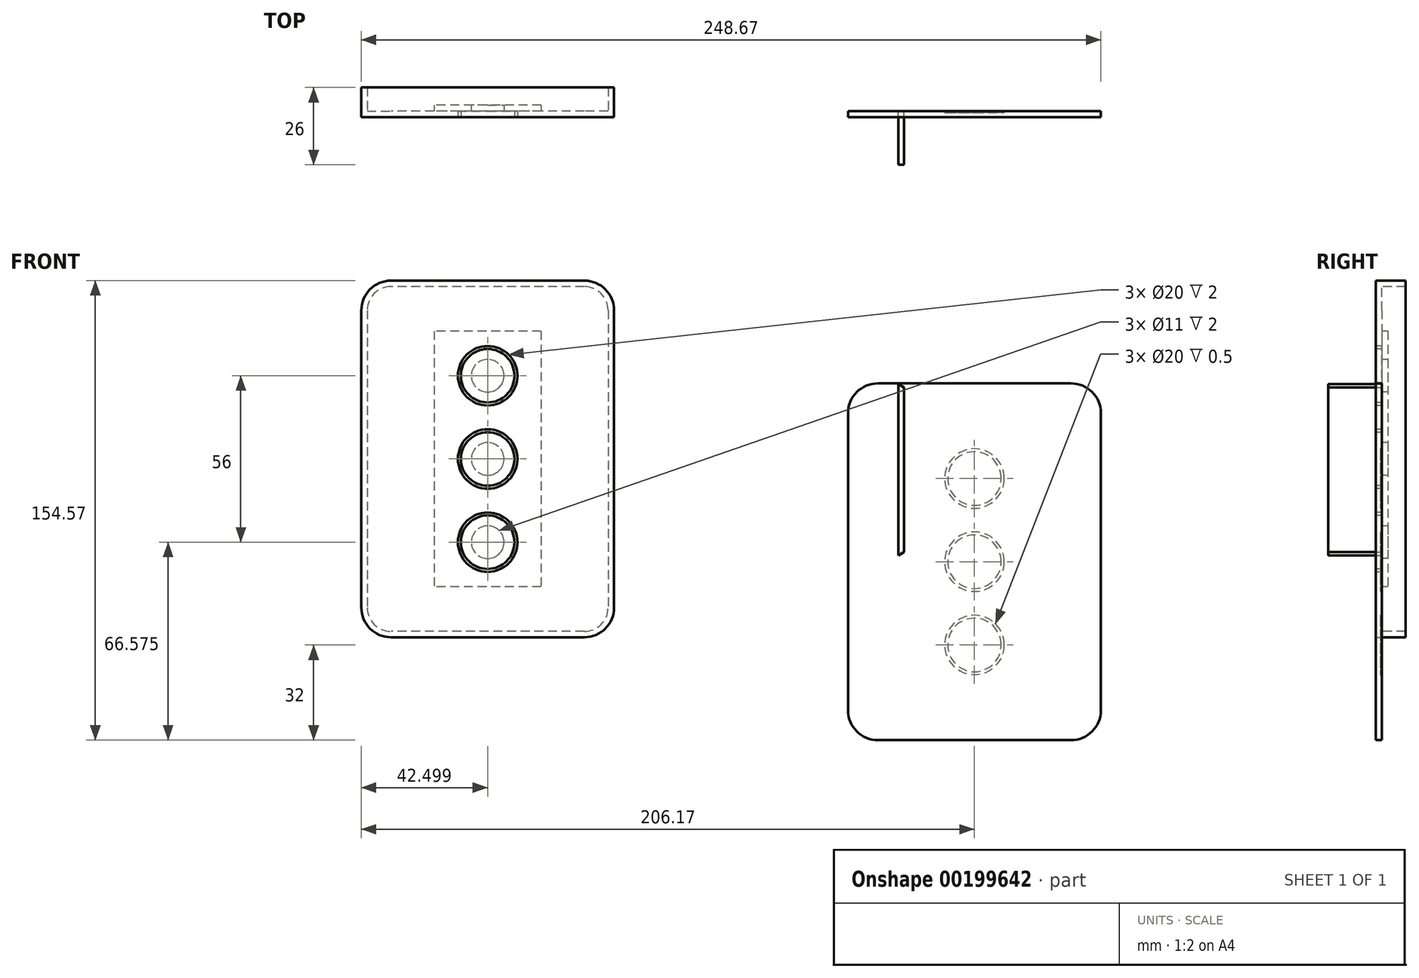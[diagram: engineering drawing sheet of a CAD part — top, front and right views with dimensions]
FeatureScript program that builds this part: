
annotation { "Feature Type Name" : "Feature", "Feature Type Description" : "" }
export const myFeature = defineFeature(function(context is Context, id is Id, definition is map)
    precondition{}
    {
        {
            var Q0;
            Q0=qCreatedBy(makeId("Front.planeOp"),FACE);
            var sketch = newSketch(context, id + "F0", { "sketchPlane" : qUnion([Q0])});
            skLineSegment(sketch, "E0.bottom", {"start": v(-32.5, 60) * mm, "end": v(32.5, 60) * mm});
            skLineSegment(sketch, "E0.top", {"start": v(-32.5, -60) * mm, "end": v(32.5, -60) * mm});
            skLineSegment(sketch, "E0.left", {"start": v(-42.5, 50) * mm, "end": v(-42.5, -50) * mm});
            skLineSegment(sketch, "E0.right", {"start": v(42.5, 50) * mm, "end": v(42.5, -50) * mm});
            skPoint(sketch, "E0.middle", {"position": v(0, 0) * mm});
            skPoint(sketch, "E1.visualSharp", {"position": v(-42.5, 60) * mm});
            skArc(sketch, "E1.filletArc", {"start": v(-32.5, 60) * mm, "mid": v(-39.57, 57.07) * mm, "end": v(-42.5, 50) * mm});
            skPoint(sketch, "E2.visualSharp", {"position": v(42.5, 60) * mm});
            skArc(sketch, "E2.filletArc", {"start": v(42.5, 50) * mm, "mid": v(39.57, 57.07) * mm, "end": v(32.5, 60) * mm});
            skPoint(sketch, "E3.visualSharp", {"position": v(42.5, -60) * mm});
            skArc(sketch, "E3.filletArc", {"start": v(32.5, -60) * mm, "mid": v(39.57, -57.07) * mm, "end": v(42.5, -50) * mm});
            skPoint(sketch, "E4.visualSharp", {"position": v(-42.5, -60) * mm});
            skArc(sketch, "E4.filletArc", {"start": v(-42.5, -50) * mm, "mid": v(-39.57, -57.07) * mm, "end": v(-32.5, -60) * mm});
            skSolve(sketch);
        }
        {
            var Q0;
            Q0=makeQuery(id+"F0.imprint","IMPRINT",FACE,{"disambiguationData":[TD([[makeQuery(id+"F0.imprint","IMPRINT",EDGE,{"derivedFrom":sQuery(id+"F0.wireOp",EDGE,"E0.bottom")}),-1.0]])]});
            extrude(context, id + "F1", {"entities" : qUnion([Q0]), "depth" : 2 * mm, "offsetDistance" : 25 * mm});
        }
        {
            var Q0;
            Q0=makeQuery(id+"F1.opExtrude","CAP_FACE",FACE,{"disambiguationData":[OSD([sQuery(id+"F0.wireOp",EDGE,"E0.bottom"),sQuery(id+"F0.wireOp",EDGE,"E0.top"),sQuery(id+"F0.wireOp",EDGE,"E0.left"),sQuery(id+"F0.wireOp",EDGE,"E0.right"),sQuery(id+"F0.wireOp",EDGE,"E1.filletArc"),sQuery(id+"F0.wireOp",EDGE,"E2.filletArc"),sQuery(id+"F0.wireOp",EDGE,"E3.filletArc"),sQuery(id+"F0.wireOp",EDGE,"E4.filletArc")])],"isStart":true});
            var sketch = newSketch(context, id + "F2", { "sketchPlane" : qUnion([Q0])});
            skCircle(sketch, "E5", {"center": v(0, 28) * mm, "radius": 10 * mm});
            skCircle(sketch, "E6", {"center": v(0, 0) * mm, "radius": 10 * mm});
            skCircle(sketch, "E7", {"center": v(0, -28) * mm, "radius": 10 * mm});
            skCircle(sketch, "E8", {"center": v(0, 28) * mm, "radius": 9 * mm});
            skCircle(sketch, "E9", {"center": v(0, 0) * mm, "radius": 9 * mm});
            skCircle(sketch, "E10", {"center": v(0, -28) * mm, "radius": 9 * mm});
            skLineSegment(sketch, "E11", {"start": v(-58.87, 60) * mm, "end": v(-58.87, -60) * mm});
            skLineSegment(sketch, "E12", {"start": v(-42.5, -66.9) * mm, "end": v(42.5, -66.9) * mm});
            skSolve(sketch);
        }
        {
            var Q0;
            Q0=makeQuery(id+"F2.imprint","IMPRINT",FACE,{"disambiguationData":[TD([[makeQuery(id+"F2.imprint","IMPRINT",EDGE,{"derivedFrom":sQuery(id+"F2.wireOp",EDGE,"E5")}),1.0]])]});
            var Q1;
            Q1=makeQuery(id+"F2.imprint","IMPRINT",FACE,{"disambiguationData":[TD([[makeQuery(id+"F2.imprint","IMPRINT",EDGE,{"derivedFrom":sQuery(id+"F2.wireOp",EDGE,"E6")}),1.0]])]});
            var Q2;
            Q2=makeQuery(id+"F2.imprint","IMPRINT",FACE,{"disambiguationData":[TD([[makeQuery(id+"F2.imprint","IMPRINT",EDGE,{"derivedFrom":sQuery(id+"F2.wireOp",EDGE,"E7")}),1.0]])]});
            extrude(context, id + "F3", {"entities" : qUnion([Q0, Q1, Q2]), "operationType" : NewBodyOperationType.REMOVE, "oppositeDirection" : true, "depth" : 0.5 * mm, "offsetDistance" : 25 * mm});
        }
        {
            var Q0;
            Q0=qCreatedBy(makeId("Front.planeOp"),FACE);
            var sketch = newSketch(context, id + "F4", { "sketchPlane" : qUnion([Q0])});
            skLineSegment(sketch, "E13", {"start": v(-25.64, 59.8) * mm, "end": v(-25.64, 2.07) * mm});
            skLineSegment(sketch, "E14", {"start": v(-23.64, 58.65) * mm, "end": v(-23.64, 3.23) * mm});
            skLineSegment(sketch, "E15", {"start": v(-23.64, 58.65) * mm, "end": v(-25.64, 59.8) * mm});
            skLineSegment(sketch, "E16", {"start": v(-25.64, 2.07) * mm, "end": v(-23.64, 3.23) * mm});
            skSolve(sketch);
        }
        {
            var Q0;
            Q0 = qSketchRegion(id + "F4", true);
            extrude(context, id + "F5", {"entities" : qUnion([Q0]), "depth" : 18 * mm, "offsetDistance" : 25 * mm});
        }
        {
            var Q0;
            Q0=qCreatedBy(makeId("Front.planeOp"),FACE);
            var sketch = newSketch(context, id + "F6", { "sketchPlane" : qUnion([Q0])});
            skLineSegment(sketch, "E17.bottom", {"start": v(-131.17, 94.57) * mm, "end": v(-196.17, 94.57) * mm});
            skLineSegment(sketch, "E17.top", {"start": v(-131.17, -25.43) * mm, "end": v(-196.17, -25.43) * mm});
            skLineSegment(sketch, "E17.left", {"start": v(-121.17, 84.57) * mm, "end": v(-121.17, -15.43) * mm});
            skLineSegment(sketch, "E17.right", {"start": v(-206.17, 84.57) * mm, "end": v(-206.17, -15.43) * mm});
            skArc(sketch, "E18.filletArc", {"start": v(-121.17, 84.57) * mm, "mid": v(-124.1, 91.65) * mm, "end": v(-131.17, 94.57) * mm});
            skArc(sketch, "E19.filletArc", {"start": v(-196.17, 94.57) * mm, "mid": v(-203.24, 91.65) * mm, "end": v(-206.17, 84.57) * mm});
            skArc(sketch, "E20.filletArc", {"start": v(-206.17, -15.43) * mm, "mid": v(-203.24, -22.5) * mm, "end": v(-196.17, -25.43) * mm});
            skArc(sketch, "E21.filletArc", {"start": v(-131.17, -25.43) * mm, "mid": v(-124.1, -22.5) * mm, "end": v(-121.17, -15.43) * mm});
            skSolve(sketch);
        }
        {
            var Q0;
            Q0=makeQuery(id+"F6.imprint","IMPRINT",FACE,{"disambiguationData":[TD([[makeQuery(id+"F6.imprint","IMPRINT",EDGE,{"derivedFrom":sQuery(id+"F6.wireOp",EDGE,"E17.bottom")}),1.0]])]});
            extrude(context, id + "F7", {"entities" : qUnion([Q0]), "depth" : 2 * mm, "offsetDistance" : 25 * mm});
        }
        {
            var Q0;
            Q0=makeQuery(id+"F7.opExtrude","CAP_FACE",FACE,{"disambiguationData":[OSD([sQuery(id+"F6.wireOp",EDGE,"E17.bottom"),sQuery(id+"F6.wireOp",EDGE,"E17.top"),sQuery(id+"F6.wireOp",EDGE,"E17.left"),sQuery(id+"F6.wireOp",EDGE,"E17.right"),sQuery(id+"F6.wireOp",EDGE,"E18.filletArc"),sQuery(id+"F6.wireOp",EDGE,"E19.filletArc"),sQuery(id+"F6.wireOp",EDGE,"E20.filletArc"),sQuery(id+"F6.wireOp",EDGE,"E21.filletArc")])],"isStart":true});
            var sketch = newSketch(context, id + "F8", { "sketchPlane" : qUnion([Q0])});
            skLineSegment(sketch, "E22.bottom", {"start": v(131.17, 92.57) * mm, "end": v(196.17, 92.57) * mm});
            skLineSegment(sketch, "E22.top", {"start": v(131.17, -23.43) * mm, "end": v(196.17, -23.43) * mm});
            skLineSegment(sketch, "E22.left", {"start": v(123.17, 84.57) * mm, "end": v(123.17, -15.43) * mm});
            skLineSegment(sketch, "E22.right", {"start": v(204.17, 84.57) * mm, "end": v(204.17, -15.43) * mm});
            skArc(sketch, "E23.filletArc", {"start": v(131.17, 92.57) * mm, "mid": v(125.51, 90.23) * mm, "end": v(123.17, 84.57) * mm});
            skArc(sketch, "E24.filletArc", {"start": v(204.17, 84.57) * mm, "mid": v(201.83, 90.23) * mm, "end": v(196.17, 92.57) * mm});
            skArc(sketch, "E25.filletArc", {"start": v(196.17, -23.43) * mm, "mid": v(201.83, -21.08) * mm, "end": v(204.17, -15.43) * mm});
            skArc(sketch, "E26.filletArc", {"start": v(123.17, -15.43) * mm, "mid": v(125.51, -21.08) * mm, "end": v(131.17, -23.43) * mm});
            skSolve(sketch);
        }
        {
            var Q0;
            Q0=makeQuery(id+"F8.imprint","IMPRINT",FACE,{"disambiguationData":[TD([[makeQuery(id+"F8.imprint","IMPRINT",EDGE,{"derivedFrom":sQuery(id+"F8.wireOp",EDGE,"E22.bottom")}),1.0]])]});
            extrude(context, id + "F9", {"entities" : qUnion([Q0]), "operationType" : NewBodyOperationType.ADD, "depth" : 8 * mm, "offsetDistance" : 25 * mm});
        }
        {
            var Q0;
            Q0=makeQuery(id+"F7.opExtrude","CAP_FACE",FACE,{"disambiguationData":[OSD([sQuery(id+"F6.wireOp",EDGE,"E17.bottom"),sQuery(id+"F6.wireOp",EDGE,"E17.top"),sQuery(id+"F6.wireOp",EDGE,"E17.left"),sQuery(id+"F6.wireOp",EDGE,"E17.right"),sQuery(id+"F6.wireOp",EDGE,"E18.filletArc"),sQuery(id+"F6.wireOp",EDGE,"E19.filletArc"),sQuery(id+"F6.wireOp",EDGE,"E20.filletArc"),sQuery(id+"F6.wireOp",EDGE,"E21.filletArc")])],"isStart":false});
            var sketch = newSketch(context, id + "F10", { "sketchPlane" : qUnion([Q0])});
            skCircle(sketch, "E27", {"center": v(-163.67, 62.57) * mm, "radius": 9 * mm});
            skCircle(sketch, "E28", {"center": v(-163.67, 34.57) * mm, "radius": 9 * mm});
            skCircle(sketch, "E29", {"center": v(-163.67, 6.57) * mm, "radius": 9 * mm});
            skCircle(sketch, "E30", {"center": v(-163.67, 62.57) * mm, "radius": 10 * mm});
            skCircle(sketch, "E31", {"center": v(-163.67, 34.57) * mm, "radius": 10 * mm});
            skCircle(sketch, "E32", {"center": v(-163.67, 6.57) * mm, "radius": 10 * mm});
            skSolve(sketch);
        }
        {
            var Q0;
            Q0 = qSketchRegion(id + "F10", true);
            extrude(context, id + "F11", {"entities" : qUnion([Q0]), "operationType" : NewBodyOperationType.REMOVE, "oppositeDirection" : true, "depth" : 25 * mm, "offsetDistance" : 25 * mm});
        }
        {
            var Q0;
            Q0=makeQuery(id+"F11.boolean.opBoolean","SPLIT",FACE,{"disambiguationData":[TD([makeQuery(id+"F9.opExtrude","SWEPT_FACE",FACE,{"disambiguationData":[OSD([sQuery(id+"F8.wireOp",EDGE,"E22.bottom")])]})])],"derivedFrom":makeQuery(id+"F7.opExtrude","CAP_FACE",FACE,{"disambiguationData":[OSD([sQuery(id+"F6.wireOp",EDGE,"E17.bottom"),sQuery(id+"F6.wireOp",EDGE,"E17.top"),sQuery(id+"F6.wireOp",EDGE,"E17.left"),sQuery(id+"F6.wireOp",EDGE,"E17.right"),sQuery(id+"F6.wireOp",EDGE,"E18.filletArc"),sQuery(id+"F6.wireOp",EDGE,"E19.filletArc"),sQuery(id+"F6.wireOp",EDGE,"E20.filletArc"),sQuery(id+"F6.wireOp",EDGE,"E21.filletArc")])],"isStart":true})});
            var sketch = newSketch(context, id + "F12", { "sketchPlane" : qUnion([Q0])});
            skLineSegment(sketch, "E33.bottom", {"start": v(145.67, 77.57) * mm, "end": v(181.67, 77.57) * mm});
            skLineSegment(sketch, "E33.top", {"start": v(145.67, -8.43) * mm, "end": v(181.67, -8.43) * mm});
            skLineSegment(sketch, "E33.left", {"start": v(145.67, 77.57) * mm, "end": v(145.67, -8.43) * mm});
            skLineSegment(sketch, "E33.right", {"start": v(181.67, 77.57) * mm, "end": v(181.67, -8.43) * mm});
            skPoint(sketch, "E34.start.orphan", {"position": v(163.67, 62.57) * mm});
            skPoint(sketch, "E35.end.orphan", {"position": v(163.67, -8.43) * mm});
            skPoint(sketch, "E35.start.orphan", {"position": v(163.67, 6.57) * mm});
            skSolve(sketch);
        }
        {
            var Q0;
            Q0=makeQuery(id+"F12.imprint","IMPRINT",FACE,{"disambiguationData":[TD([[makeQuery(id+"F12.imprint","IMPRINT",EDGE,{"derivedFrom":makeQuery(id+"F11.boolean.opBoolean","INTERSECT",EDGE,{"derivedFrom":[makeQuery(id+"F7.opExtrude","CAP_FACE",FACE,{"disambiguationData":[OSD([sQuery(id+"F6.wireOp",EDGE,"E17.bottom"),sQuery(id+"F6.wireOp",EDGE,"E17.top"),sQuery(id+"F6.wireOp",EDGE,"E17.left"),sQuery(id+"F6.wireOp",EDGE,"E17.right"),sQuery(id+"F6.wireOp",EDGE,"E18.filletArc"),sQuery(id+"F6.wireOp",EDGE,"E19.filletArc"),sQuery(id+"F6.wireOp",EDGE,"E20.filletArc"),sQuery(id+"F6.wireOp",EDGE,"E21.filletArc")])],"isStart":true}),makeQuery(id+"F11.opExtrude","SWEPT_FACE",FACE,{"disambiguationData":[OSD([sQuery(id+"F10.wireOp",EDGE,"E30")])]})]})}),-1.0]])]});
            var Q1;
            Q1=makeQuery(id+"F12.imprint","IMPRINT",FACE,{"disambiguationData":[TD([[makeQuery(id+"F12.imprint","IMPRINT",EDGE,{"derivedFrom":makeQuery(id+"F11.boolean.opBoolean","INTERSECT",EDGE,{"derivedFrom":[makeQuery(id+"F7.opExtrude","CAP_FACE",FACE,{"disambiguationData":[OSD([sQuery(id+"F6.wireOp",EDGE,"E17.bottom"),sQuery(id+"F6.wireOp",EDGE,"E17.top"),sQuery(id+"F6.wireOp",EDGE,"E17.left"),sQuery(id+"F6.wireOp",EDGE,"E17.right"),sQuery(id+"F6.wireOp",EDGE,"E18.filletArc"),sQuery(id+"F6.wireOp",EDGE,"E19.filletArc"),sQuery(id+"F6.wireOp",EDGE,"E20.filletArc"),sQuery(id+"F6.wireOp",EDGE,"E21.filletArc")])],"isStart":true}),makeQuery(id+"F11.opExtrude","SWEPT_FACE",FACE,{"disambiguationData":[OSD([sQuery(id+"F10.wireOp",EDGE,"E31")])]})]})}),-1.0]])]});
            var Q2;
            Q2=makeQuery(id+"F12.imprint","IMPRINT",FACE,{"disambiguationData":[TD([[makeQuery(id+"F12.imprint","IMPRINT",EDGE,{"derivedFrom":makeQuery(id+"F11.boolean.opBoolean","INTERSECT",EDGE,{"derivedFrom":[makeQuery(id+"F7.opExtrude","CAP_FACE",FACE,{"disambiguationData":[OSD([sQuery(id+"F6.wireOp",EDGE,"E17.bottom"),sQuery(id+"F6.wireOp",EDGE,"E17.top"),sQuery(id+"F6.wireOp",EDGE,"E17.left"),sQuery(id+"F6.wireOp",EDGE,"E17.right"),sQuery(id+"F6.wireOp",EDGE,"E18.filletArc"),sQuery(id+"F6.wireOp",EDGE,"E19.filletArc"),sQuery(id+"F6.wireOp",EDGE,"E20.filletArc"),sQuery(id+"F6.wireOp",EDGE,"E21.filletArc")])],"isStart":true}),makeQuery(id+"F11.opExtrude","SWEPT_FACE",FACE,{"disambiguationData":[OSD([sQuery(id+"F10.wireOp",EDGE,"E32")])]})]})}),-1.0]])]});
            var Q3;
            Q3=makeQuery(id+"F12.imprint","IMPRINT",FACE,{"disambiguationData":[TD([[makeQuery(id+"F12.imprint","IMPRINT",EDGE,{"derivedFrom":sQuery(id+"F12.wireOp",EDGE,"E33.bottom")}),-1.0]])]});
            extrude(context, id + "F13", {"entities" : qUnion([Q0, Q1, Q2, Q3]), "operationType" : NewBodyOperationType.ADD, "depth" : 2 * mm, "offsetDistance" : 25 * mm});
        }
        {
            var Q0;
            Q0=makeQuery(id+"F13.boolean.opBoolean","SPLIT",FACE,{"disambiguationData":[TD([makeQuery(id+"F11.boolean.opBoolean","COPY",FACE,{"derivedFrom":makeQuery(id+"F11.opExtrude","SWEPT_FACE",FACE,{"disambiguationData":[OSD([sQuery(id+"F10.wireOp",EDGE,"E30")])]})})])],"derivedFrom":makeQuery(id+"F13.opExtrude","CAP_FACE",FACE,{"disambiguationData":[OSD([sQuery(id+"F12.wireOp",EDGE,"E33.bottom"),sQuery(id+"F12.wireOp",EDGE,"E33.top"),sQuery(id+"F12.wireOp",EDGE,"E33.left"),sQuery(id+"F12.wireOp",EDGE,"E33.right")])],"isStart":true})});
            var sketch = newSketch(context, id + "F14", { "sketchPlane" : qUnion([Q0])});
            skCircle(sketch, "E36", {"center": v(-163.67, 62.57) * mm, "radius": 5.5 * mm});
            skSolve(sketch);
        }
        {
            var Q0;
            Q0=makeQuery(id+"F13.boolean.opBoolean","SPLIT",FACE,{"disambiguationData":[TD([makeQuery(id+"F11.boolean.opBoolean","COPY",FACE,{"derivedFrom":makeQuery(id+"F11.opExtrude","SWEPT_FACE",FACE,{"disambiguationData":[OSD([sQuery(id+"F10.wireOp",EDGE,"E31")])]})})])],"derivedFrom":makeQuery(id+"F13.opExtrude","CAP_FACE",FACE,{"disambiguationData":[OSD([sQuery(id+"F12.wireOp",EDGE,"E33.bottom"),sQuery(id+"F12.wireOp",EDGE,"E33.top"),sQuery(id+"F12.wireOp",EDGE,"E33.left"),sQuery(id+"F12.wireOp",EDGE,"E33.right")])],"isStart":true})});
            var sketch = newSketch(context, id + "F15", { "sketchPlane" : qUnion([Q0])});
            skCircle(sketch, "E37", {"center": v(-163.67, 34.57) * mm, "radius": 5.5 * mm});
            skSolve(sketch);
        }
        {
            var Q0;
            Q0=makeQuery(id+"F13.boolean.opBoolean","SPLIT",FACE,{"disambiguationData":[TD([makeQuery(id+"F11.boolean.opBoolean","COPY",FACE,{"derivedFrom":makeQuery(id+"F11.opExtrude","SWEPT_FACE",FACE,{"disambiguationData":[OSD([sQuery(id+"F10.wireOp",EDGE,"E32")])]})})])],"derivedFrom":makeQuery(id+"F13.opExtrude","CAP_FACE",FACE,{"disambiguationData":[OSD([sQuery(id+"F12.wireOp",EDGE,"E33.bottom"),sQuery(id+"F12.wireOp",EDGE,"E33.top"),sQuery(id+"F12.wireOp",EDGE,"E33.left"),sQuery(id+"F12.wireOp",EDGE,"E33.right")])],"isStart":true})});
            var sketch = newSketch(context, id + "F16", { "sketchPlane" : qUnion([Q0])});
            skCircle(sketch, "E38", {"center": v(-163.67, 6.57) * mm, "radius": 5.5 * mm});
            skSolve(sketch);
        }
        {
            var Q0;
            Q0=makeQuery(id+"F14.imprint","IMPRINT",FACE,{"disambiguationData":[TD([[makeQuery(id+"F14.imprint","IMPRINT",EDGE,{"derivedFrom":sQuery(id+"F14.wireOp",EDGE,"E36")}),1.0]])]});
            var Q1;
            Q1=makeQuery(id+"F15.imprint","IMPRINT",FACE,{"disambiguationData":[TD([[makeQuery(id+"F15.imprint","IMPRINT",EDGE,{"derivedFrom":sQuery(id+"F15.wireOp",EDGE,"E37")}),1.0]])]});
            var Q2;
            Q2=makeQuery(id+"F16.imprint","IMPRINT",FACE,{"disambiguationData":[TD([[makeQuery(id+"F16.imprint","IMPRINT",EDGE,{"derivedFrom":sQuery(id+"F16.wireOp",EDGE,"E38")}),1.0]])]});
            extrude(context, id + "F17", {"entities" : qUnion([Q0, Q1, Q2]), "operationType" : NewBodyOperationType.REMOVE, "oppositeDirection" : true, "depth" : 25 * mm, "offsetDistance" : 25 * mm});
        }
    });
